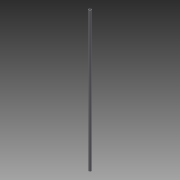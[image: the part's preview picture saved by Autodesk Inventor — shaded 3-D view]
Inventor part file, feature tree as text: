
AUTODESK INVENTOR PART (.ipt)
format: ipt  version: 2013 (Build 170138000, 138)  size: 64,512 bytes
history: native  units: in
note: dims shown in document units (in); Inventor stores cm internally (conversion verified against a paired STEP export)
features: extrude x1, sketch x1
ambient origin geometry x8: Origin, YZ Plane, XZ Plane, XY Plane, X Axis, Y Axis, Z Axis, Center Point
bodies: Solid1 (feature_tree)
feature tree (2):
  extrude  "Extrusion1"  Depth=0.0625in
  sketch  "Sketch1"  dims[d0=0.5in d2=0.0625in d3=30.0in d4=0.0in]
